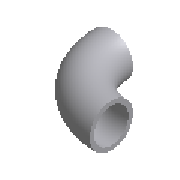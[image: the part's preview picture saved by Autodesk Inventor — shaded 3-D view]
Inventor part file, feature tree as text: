
AUTODESK INVENTOR PART (.ipt)
format: ipt  version: 2025 (Build 290162010, 162A)  size: 183,296 bytes
history: native  units: mm (DEFAULTED — no unit token found)
features: other x4, sweep x1
ambient origin geometry x8: Origin, YZ Plane, XZ Plane, XY Plane, X Axis, Y Axis, Z Axis, Center Point
bodies: Solid1 (feature_tree)
feature tree (5):
  sweep  "Sweep1"
  other  "Work Point1"
  other  "Work Point2"
  other  "Work Axis1"
  other  "Work Axis2"
